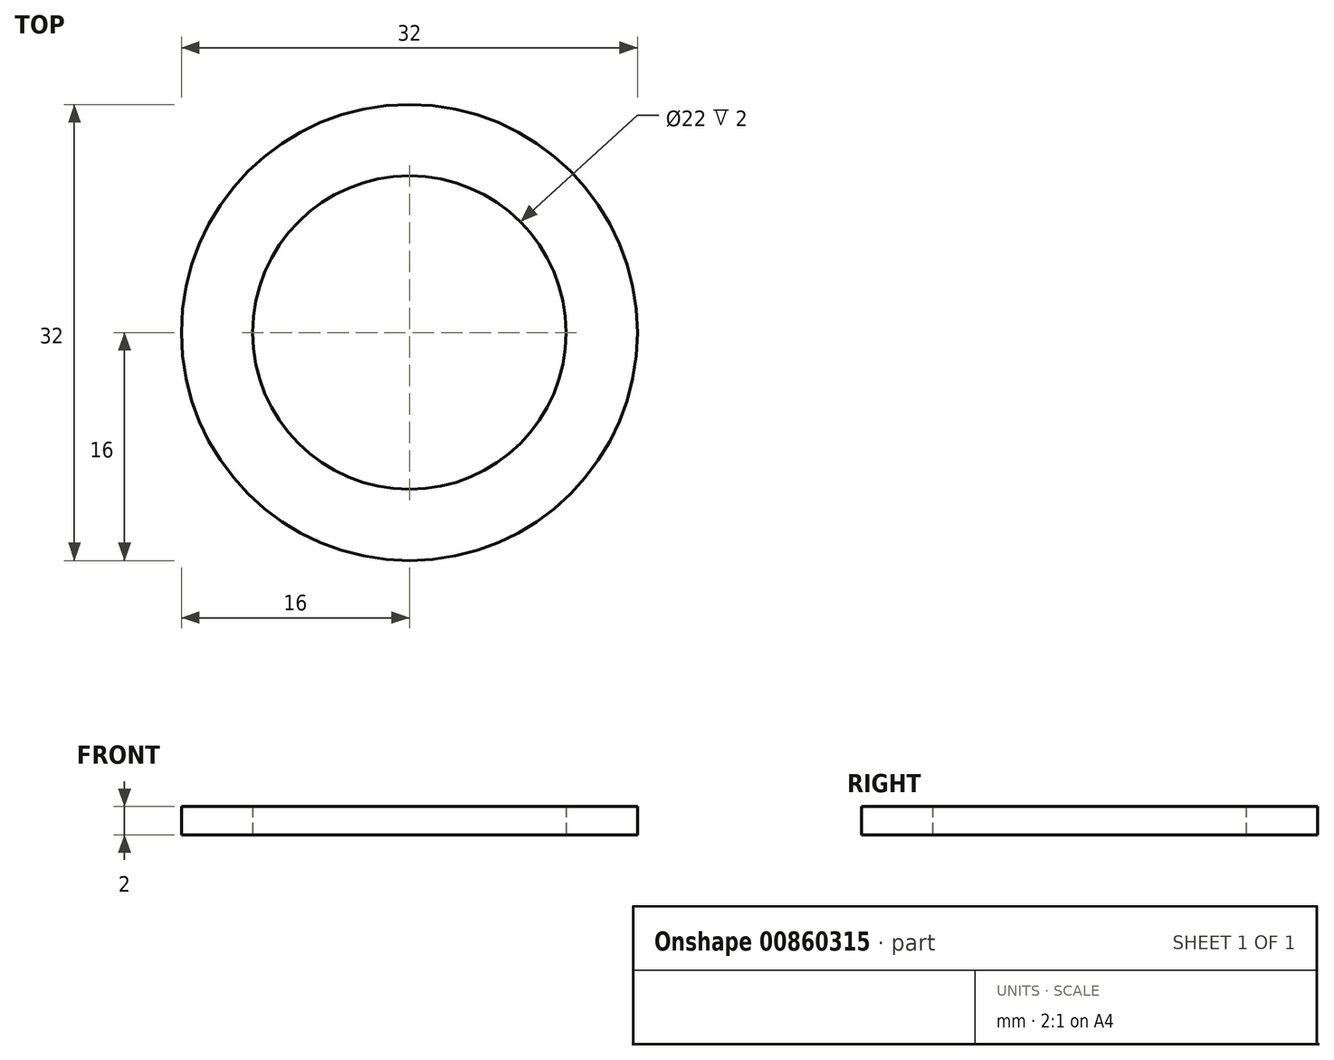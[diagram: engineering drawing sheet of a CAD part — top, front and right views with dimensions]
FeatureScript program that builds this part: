
annotation { "Feature Type Name" : "Feature", "Feature Type Description" : "" }
export const myFeature = defineFeature(function(context is Context, id is Id, definition is map)
    precondition{}
    {
        {
            var Q0;
            Q0=qCreatedBy(makeId("Top.planeOp"),FACE);
            var sketch = newSketch(context, id + "F0", { "sketchPlane" : qUnion([Q0])});
            skCircle(sketch, "E0", {"center": v(0, 0) * mm, "radius": 11 * mm});
            skCircle(sketch, "E1", {"center": v(0, 0) * mm, "radius": 16 * mm});
            skSolve(sketch);
        }
        {
            var Q0;
            Q0=makeQuery(id+"F0.imprint","IMPRINT",FACE,{"disambiguationData":[TD([[makeQuery(id+"F0.imprint","IMPRINT",EDGE,{"derivedFrom":sQuery(id+"F0.wireOp",EDGE,"E0")}),-1.0]])]});
            extrude(context, id + "F1", {"entities" : qUnion([Q0]), "depth" : 2 * mm, "offsetDistance" : 25 * mm});
        }
    });
